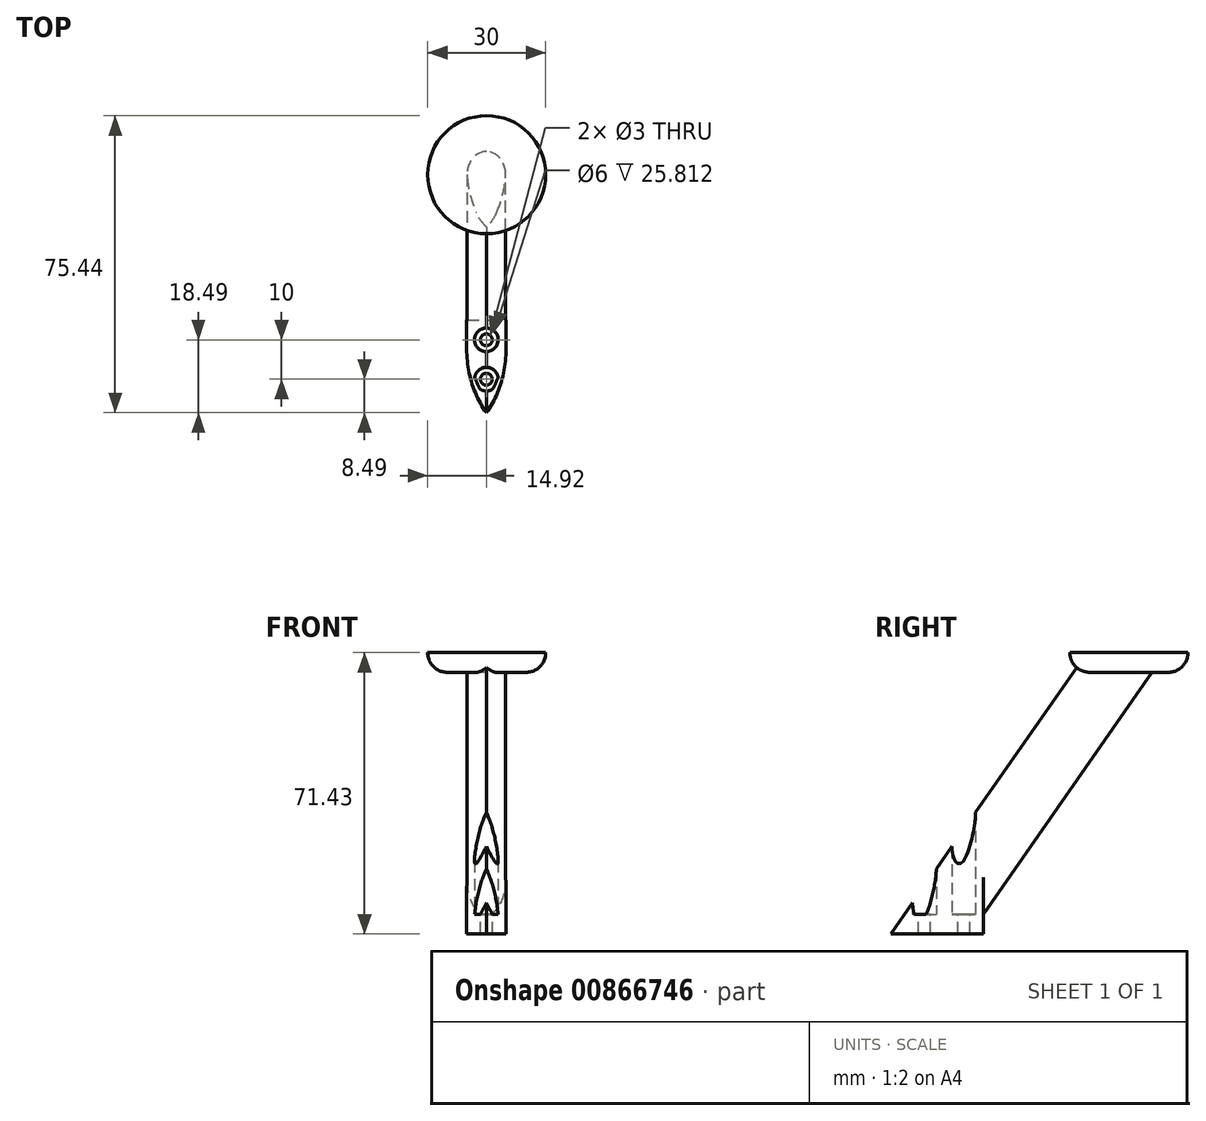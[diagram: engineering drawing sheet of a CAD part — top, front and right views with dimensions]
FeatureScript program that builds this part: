
annotation { "Feature Type Name" : "Feature", "Feature Type Description" : "" }
export const myFeature = defineFeature(function(context is Context, id is Id, definition is map)
    precondition{}
    {
        {
            var Q0;
            Q0=qCreatedBy(makeId("Top.planeOp"),FACE);
            var sketch = newSketch(context, id + "F0", { "sketchPlane" : qUnion([Q0])});
            skLineSegment(sketch, "E0.bottom", {"start": v(5, -10) * mm, "end": v(-5, -10) * mm});
            skLineSegment(sketch, "E0.top", {"start": v(5, 10) * mm, "end": v(-5, 10) * mm});
            skLineSegment(sketch, "E0.left", {"start": v(5, -10) * mm, "end": v(5, 10) * mm});
            skLineSegment(sketch, "E0.right", {"start": v(-5, -10) * mm, "end": v(-5, 10) * mm});
            skPoint(sketch, "E0.middle", {"position": v(0, 0) * mm});
            skPoint(sketch, "E1", {"position": v(0, 10) * mm});
            skPoint(sketch, "E2", {"position": v(0, -10) * mm});
            skLineSegment(sketch, "E3", {"start": v(0, 10) * mm, "end": v(0, 0) * mm});
            skLineSegment(sketch, "E4", {"start": v(0, 0) * mm, "end": v(0, -10) * mm});
            skPoint(sketch, "E5", {"position": v(0, 5) * mm});
            skPoint(sketch, "E6", {"position": v(0, -5) * mm});
            skSolve(sketch);
        }
        {
            var Q0;
            {var subQ0=sQuery(id+"F0.wireOp",EDGE,"E0.right");Q0=makeQuery(id+"F0.imprint","IMPRINT",FACE,{"disambiguationData":[TD([[makeQuery(id+"F0.imprint","IMPRINT",EDGE,{"derivedFrom":subQ0}),-1.0]])]});}
            var Q1;
            {var subQ1=sQuery(id+"F0.wireOp",EDGE,"E0.left");Q1=makeQuery(id+"F0.imprint","IMPRINT",FACE,{"disambiguationData":[TD([[makeQuery(id+"F0.imprint","IMPRINT",EDGE,{"derivedFrom":subQ1}),1.0]])]});}
            extrude(context, id + "F1", {"entities" : qUnion([Q0, Q1]), "depth" : 5 * mm, "offsetDistance" : 25 * mm});
        }
        {
            var Q0;
            Q0=makeQuery(id+"F1.opExtrude","CAP_FACE",FACE,{"disambiguationData":[OSD([sQuery(id+"F0.wireOp",EDGE,"E0.bottom"),sQuery(id+"F0.wireOp",EDGE,"E0.top"),sQuery(id+"F0.wireOp",EDGE,"E0.left"),sQuery(id+"F0.wireOp",EDGE,"E0.right")])],"isStart":false});
            var sketch = newSketch(context, id + "F2", { "sketchPlane" : qUnion([Q0])});
            skPoint(sketch, "E7", {"position": v(0, 10) * mm});
            skPoint(sketch, "E8", {"position": v(0, -10) * mm});
            skPoint(sketch, "E9", {"position": v(0, 0) * mm});
            skLineSegment(sketch, "E10", {"start": v(0, 10) * mm, "end": v(0, 0) * mm});
            skLineSegment(sketch, "E11", {"start": v(0, 0) * mm, "end": v(0, -10) * mm});
            skPoint(sketch, "E12", {"position": v(0, 5) * mm});
            skPoint(sketch, "E13", {"position": v(0, -5) * mm});
            skSolve(sketch);
        }
        {
            var Q0;
            Q0=qCreatedBy(makeId("Right.planeOp"),FACE);
            var sketch = newSketch(context, id + "F3", { "sketchPlane" : qUnion([Q0])});
            skLineSegment(sketch, "E14", {"start": v(0, 0) * mm, "end": v(46.33, 66.43) * mm});
            skSolve(sketch);
        }
        {
            var Q0;
            Q0=makeQuery(id+"F1.opExtrude","CAP_FACE",FACE,{"disambiguationData":[OSD([sQuery(id+"F0.wireOp",EDGE,"E0.bottom"),sQuery(id+"F0.wireOp",EDGE,"E0.top"),sQuery(id+"F0.wireOp",EDGE,"E0.left"),sQuery(id+"F0.wireOp",EDGE,"E0.right")])],"isStart":false});
            var Q1;
            Q1=sQuery(id+"F3.wireOp",EDGE,"E14");
            sweep(context, id + "F4", {"operationType" : NewBodyOperationType.ADD, "profiles" : qUnion([Q0]), "path" : qUnion([Q1])});
        }
        {
            var Q0;
            Q0=makeQuery(id+"F4.opSweep","SWEPT_EDGE",EDGE,{"disambiguationData":[OSD([sQuery(id+"F0.wireOp",EDGE,"E0.bottom"),sQuery(id+"F0.wireOp",EDGE,"E0.left"),sQuery(id+"F3.wireOp",EDGE,"E14")])]});
            var Q1;
            Q1=makeQuery(id+"F4.opSweep","SWEPT_EDGE",EDGE,{"disambiguationData":[OSD([sQuery(id+"F0.wireOp",EDGE,"E0.bottom"),sQuery(id+"F0.wireOp",EDGE,"E0.right"),sQuery(id+"F3.wireOp",EDGE,"E14")])]});
            chamfer(context, id + "F5", {"entities" : qUnion([Q0, Q1]), "width" : 5 * mm, "tangentPropagation" : true});
        }
        {
            var Q0;
            {var subQ0=sQuery(id+"F3.wireOp",EDGE,"E14");var subQ1=sQuery(id+"F0.wireOp",EDGE,"E0.left");Q0=makeQuery(id+"F5.opChamfer","BLEND_EDGE",EDGE,{"blendedFrom":[makeQuery(id+"F4.opSweep","SWEPT_EDGE",EDGE,{"disambiguationData":[OSD([sQuery(id+"F0.wireOp",EDGE,"E0.bottom"),subQ1,subQ0])]}),makeQuery(id+"F4.boolean.opBoolean","MERGE",FACE,{"derivedFrom":[makeQuery(id+"F1.opExtrude","SWEPT_FACE",FACE,{"disambiguationData":[OSD([subQ1])]}),makeQuery(id+"F4.opSweep","SWEPT_FACE",FACE,{"disambiguationData":[OSD([subQ1,subQ0])]})]})],"blendedInto":[makeQuery(id+"F4.boolean.opBoolean","MERGE",FACE,{"derivedFrom":[makeQuery(id+"F1.opExtrude","SWEPT_FACE",FACE,{"disambiguationData":[OSD([subQ1])]}),makeQuery(id+"F4.opSweep","SWEPT_FACE",FACE,{"disambiguationData":[OSD([subQ1,subQ0])]})]})]});}
            var Q1;
            {var subQ0=sQuery(id+"F3.wireOp",EDGE,"E14");var subQ1=sQuery(id+"F0.wireOp",EDGE,"E0.right");Q1=makeQuery(id+"F5.opChamfer","BLEND_EDGE",EDGE,{"blendedFrom":[makeQuery(id+"F4.opSweep","SWEPT_EDGE",EDGE,{"disambiguationData":[OSD([sQuery(id+"F0.wireOp",EDGE,"E0.bottom"),subQ1,subQ0])]}),makeQuery(id+"F4.boolean.opBoolean","MERGE",FACE,{"derivedFrom":[makeQuery(id+"F1.opExtrude","SWEPT_FACE",FACE,{"disambiguationData":[OSD([subQ1])]}),makeQuery(id+"F4.opSweep","SWEPT_FACE",FACE,{"disambiguationData":[OSD([subQ1,subQ0])]})]})],"blendedInto":[makeQuery(id+"F4.boolean.opBoolean","MERGE",FACE,{"derivedFrom":[makeQuery(id+"F1.opExtrude","SWEPT_FACE",FACE,{"disambiguationData":[OSD([subQ1])]}),makeQuery(id+"F4.opSweep","SWEPT_FACE",FACE,{"disambiguationData":[OSD([subQ1,subQ0])]})]})]});}
            fillet(context, id + "F6", {"entities" : qUnion([Q0, Q1]), "radius" : 20 * mm, "tangentPropagation" : true, "allowEdgeOverflow" : false});
        }
        {
            var Q0;
            Q0=makeQuery(id+"F4.opSweep","SWEPT_EDGE",EDGE,{"disambiguationData":[OSD([sQuery(id+"F0.wireOp",EDGE,"E0.top"),sQuery(id+"F0.wireOp",EDGE,"E0.left"),sQuery(id+"F3.wireOp",EDGE,"E14")])]});
            var Q1;
            Q1=makeQuery(id+"F4.opSweep","SWEPT_EDGE",EDGE,{"disambiguationData":[OSD([sQuery(id+"F0.wireOp",EDGE,"E0.top"),sQuery(id+"F0.wireOp",EDGE,"E0.right"),sQuery(id+"F3.wireOp",EDGE,"E14")])]});
            fillet(context, id + "F7", {"entities" : qUnion([Q0, Q1]), "radius" : 4.83 * mm, "tangentPropagation" : true, "allowEdgeOverflow" : false});
        }
        {
            var Q0;
            Q0=sQuery(id+"F2.wireOp",VERTEX,"E13");
            var Q1;
            Q1=sQuery(id+"F2.wireOp",VERTEX,"E12");
            var Q2;
            Q2=makeQuery(id+"F1.opExtrude","SWEPT_BODY",BODY,{"disambiguationData":[OSD([sQuery(id+"F0.wireOp",EDGE,"E0.bottom"),sQuery(id+"F0.wireOp",EDGE,"E0.top"),sQuery(id+"F0.wireOp",EDGE,"E0.left"),sQuery(id+"F0.wireOp",EDGE,"E0.right")])]});
            hole(context, id + "F8", {"style" : HoleStyle.SIMPLE, "endStyle" : HoleEndStyle.BLIND, "oppositeDirection" : true, "holeDiameter" : 6 * mm, "majorDiameter" : 5 * mm, "holeDepth" : 27 * mm, "isTappedThrough" : true, "tappedDepth" : 12 * mm, "tapClearance" : 3, "startFromSketch" : true, "locations" : qUnion([Q0, Q1]), "scope" : qUnion([Q2])});
        }
        {
            var Q0;
            Q0=sQuery(id+"F2.wireOp",VERTEX,"E13");
            var Q1;
            Q1=sQuery(id+"F2.wireOp",VERTEX,"E12");
            var Q2;
            Q2=makeQuery(id+"F1.opExtrude","SWEPT_BODY",BODY,{"disambiguationData":[OSD([sQuery(id+"F0.wireOp",EDGE,"E0.bottom"),sQuery(id+"F0.wireOp",EDGE,"E0.top"),sQuery(id+"F0.wireOp",EDGE,"E0.left"),sQuery(id+"F0.wireOp",EDGE,"E0.right")])]});
            hole(context, id + "F9", {"style" : HoleStyle.SIMPLE, "endStyle" : HoleEndStyle.BLIND, "holeDiameter" : 3 * mm, "majorDiameter" : 5 * mm, "holeDepth" : 5 * mm, "isTappedThrough" : true, "tappedDepth" : 12 * mm, "tapClearance" : 3, "startFromSketch" : true, "locations" : qUnion([Q0, Q1]), "scope" : qUnion([Q2])});
        }
        {
            var Q0;
            Q0=makeQuery(id+"F4.opSweep","CAP_FACE",FACE,{"disambiguationData":[OSD([sQuery(id+"F0.wireOp",EDGE,"E0.bottom"),sQuery(id+"F0.wireOp",EDGE,"E0.top"),sQuery(id+"F0.wireOp",EDGE,"E0.left"),sQuery(id+"F0.wireOp",EDGE,"E0.right"),sQuery(id+"F3.wireOp",VERTEX,"E14.end")])],"isStart":false});
            var sketch = newSketch(context, id + "F10", { "sketchPlane" : qUnion([Q0])});
            skPoint(sketch, "E15", {"position": v(0.08, 46.95) * mm});
            skCircle(sketch, "E16", {"center": v(0.08, 46.95) * mm, "radius": 15 * mm});
            skSolve(sketch);
        }
        {
            var Q0;
            Q0 = qSketchRegion(id + "F10", true);
            extrude(context, id + "F11", {"entities" : qUnion([Q0]), "operationType" : NewBodyOperationType.ADD, "depth" : 5 * mm, "offsetDistance" : 25 * mm});
        }
        {
            var Q0;
            Q0=makeQuery(id+"F11.opExtrude","CAP_EDGE",EDGE,{"disambiguationData":[OSD([sQuery(id+"F10.wireOp",EDGE,"E16")])],"isStart":true});
            fillet(context, id + "F12", {"entities" : qUnion([Q0]), "radius" : 5 * mm, "tangentPropagation" : true, "allowEdgeOverflow" : false});
        }
    });
